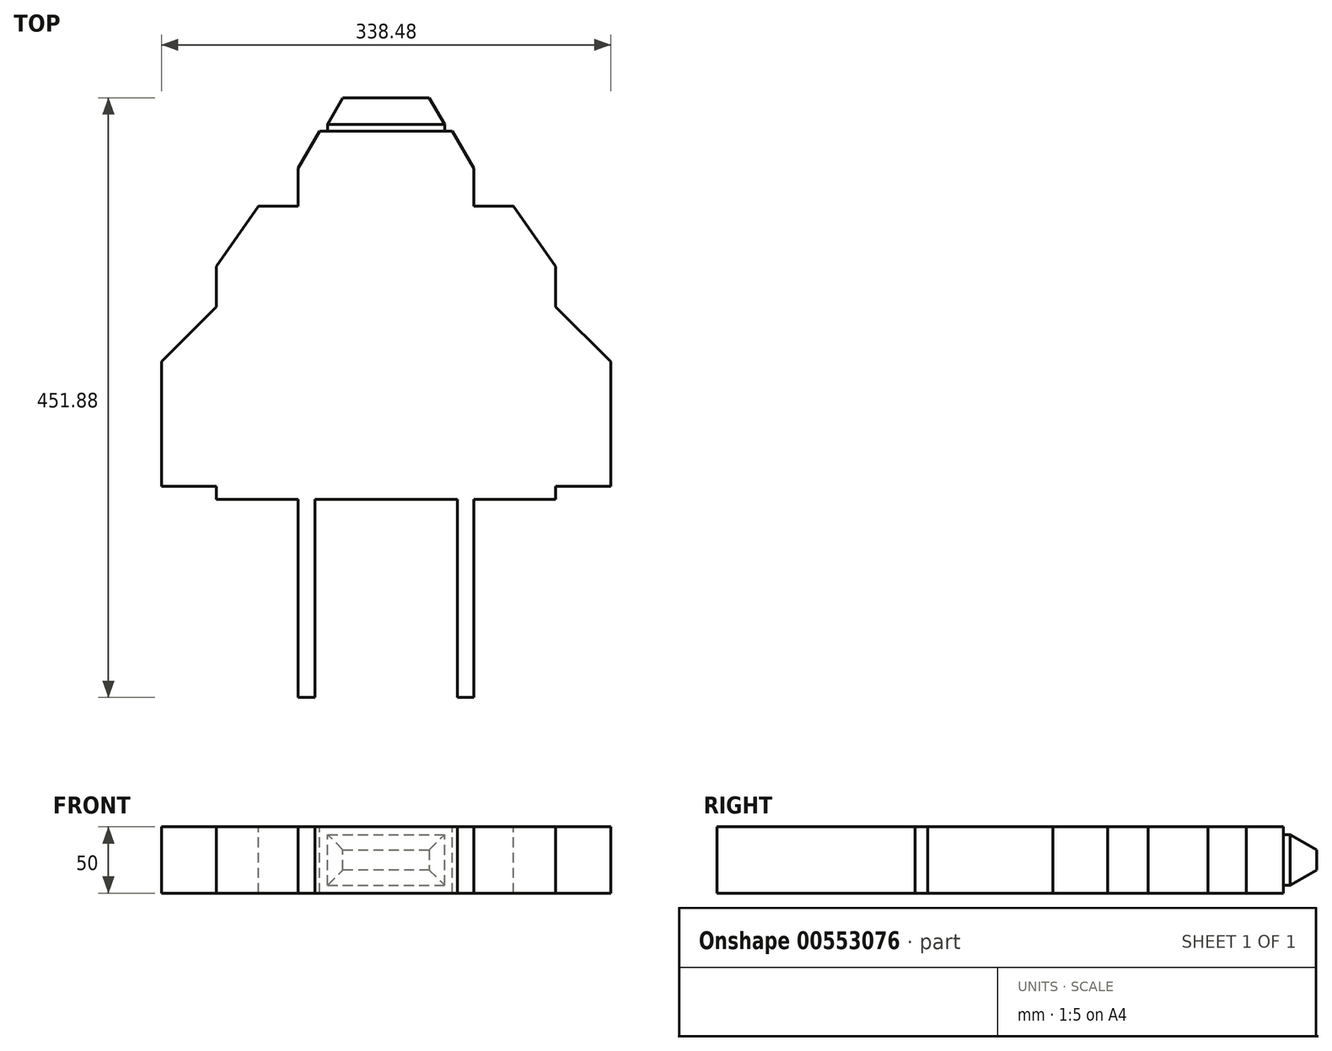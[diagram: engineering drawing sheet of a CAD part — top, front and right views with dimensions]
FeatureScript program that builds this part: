
annotation { "Feature Type Name" : "Feature", "Feature Type Description" : "" }
export const myFeature = defineFeature(function(context is Context, id is Id, definition is map)
    precondition{}
    {
        {
            var Q0;
            Q0=qCreatedBy(makeId("Top.planeOp"),FACE);
            var sketch = newSketch(context, id + "F0", { "sketchPlane" : qUnion([Q0])});
            skLineSegment(sketch, "E0", {"start": v(0, 218.46) * mm, "end": v(-50, 218.46) * mm});
            skLineSegment(sketch, "E1", {"start": v(-50, 218.46) * mm, "end": v(-66.23, 190.36) * mm});
            skLineSegment(sketch, "E2", {"start": v(-66.23, 190.36) * mm, "end": v(-66.23, 0) * mm});
            skLineSegment(sketch, "E3.MirrorCS", {"start": v(66.23, 190.36) * mm, "end": v(66.23, 0) * mm});
            skLineSegment(sketch, "E4.MirrorCS", {"start": v(0, 218.46) * mm, "end": v(50, 218.46) * mm});
            skLineSegment(sketch, "E5.MirrorCS", {"start": v(50, 218.46) * mm, "end": v(66.23, 190.36) * mm});
            skLineSegment(sketch, "E6", {"start": v(-50, 218.46) * mm, "end": v(-50, 0) * mm, "construction": true});
            skLineSegment(sketch, "E7", {"start": v(-66.23, 0) * mm, "end": v(-66.23, -208.42) * mm});
            skLineSegment(sketch, "E8", {"start": v(-66.23, -208.42) * mm, "end": v(-53.7, -208.42) * mm});
            skLineSegment(sketch, "E9", {"start": v(-53.7, -208.42) * mm, "end": v(-53.7, -59.28) * mm});
            skLineSegment(sketch, "E10", {"start": v(-53.7, -59.28) * mm, "end": v(0, -59.28) * mm});
            skLineSegment(sketch, "E11.MirrorCS", {"start": v(66.23, -208.42) * mm, "end": v(53.7, -208.42) * mm});
            skLineSegment(sketch, "E12.MirrorCS", {"start": v(66.23, 0) * mm, "end": v(66.23, -208.42) * mm});
            skLineSegment(sketch, "E13.MirrorCS", {"start": v(53.7, -59.28) * mm, "end": v(0, -59.28) * mm});
            skLineSegment(sketch, "E14.MirrorCS", {"start": v(53.7, -208.42) * mm, "end": v(53.7, -59.28) * mm});
            skLineSegment(sketch, "E15", {"start": v(-66.23, 161.65) * mm, "end": v(-96.05, 161.65) * mm});
            skLineSegment(sketch, "E16", {"start": v(-96.05, 161.65) * mm, "end": v(-127.76, 116.36) * mm});
            skLineSegment(sketch, "E17", {"start": v(-127.76, 116.36) * mm, "end": v(-127.76, -59.28) * mm});
            skLineSegment(sketch, "E18", {"start": v(-53.7, -59.28) * mm, "end": v(-66.23, -59.28) * mm, "construction": true});
            skLineSegment(sketch, "E19", {"start": v(-127.76, -59.28) * mm, "end": v(-66.23, -59.28) * mm});
            skLineSegment(sketch, "E20", {"start": v(-127.76, 86.04) * mm, "end": v(-169.24, 44.56) * mm});
            skLineSegment(sketch, "E21", {"start": v(-169.24, 44.56) * mm, "end": v(-169.24, -49.47) * mm});
            skLineSegment(sketch, "E22", {"start": v(-169.24, -49.47) * mm, "end": v(-127.76, -49.47) * mm});
            skLineSegment(sketch, "E23", {"start": v(-96.05, 161.65) * mm, "end": v(-96.05, 118.1) * mm, "construction": true});
            skLineSegment(sketch, "E24.MirrorCS", {"start": v(96.05, 161.65) * mm, "end": v(127.76, 116.36) * mm});
            skLineSegment(sketch, "E25.MirrorCS", {"start": v(127.76, 86.04) * mm, "end": v(169.24, 44.56) * mm});
            skLineSegment(sketch, "E26.MirrorCS", {"start": v(169.24, -49.47) * mm, "end": v(127.76, -49.47) * mm});
            skLineSegment(sketch, "E27.MirrorCS", {"start": v(96.05, 161.65) * mm, "end": v(96.05, 118.1) * mm, "construction": true});
            skLineSegment(sketch, "E28.MirrorCS", {"start": v(169.24, 44.56) * mm, "end": v(169.24, -49.47) * mm});
            skLineSegment(sketch, "E29.MirrorCS", {"start": v(127.76, 116.36) * mm, "end": v(127.76, -59.28) * mm});
            skLineSegment(sketch, "E30.MirrorCS", {"start": v(66.23, 161.65) * mm, "end": v(96.05, 161.65) * mm});
            skLineSegment(sketch, "E31.MirrorCS", {"start": v(127.76, -59.28) * mm, "end": v(66.23, -59.28) * mm});
            skSolve(sketch);
        }
        {
            var Q0;
            Q0=makeQuery(id+"F0.imprint","IMPRINT",FACE,{"disambiguationData":[TD([[makeQuery(id+"F0.imprint","IMPRINT",EDGE,{"derivedFrom":sQuery(id+"F0.wireOp",EDGE,"E0")}),1.0]])]});
            var Q1;
            {var subQ5=sQuery(id+"F0.wireOp",EDGE,"E15");Q1=makeQuery(id+"F0.imprint","IMPRINT",FACE,{"disambiguationData":[TD([[makeQuery(id+"F0.imprint","IMPRINT",EDGE,{"derivedFrom":subQ5}),1.0]])]});}
            var Q2;
            {var subQ0=sQuery(id+"F0.wireOp",EDGE,"E20");Q2=makeQuery(id+"F0.imprint","IMPRINT",FACE,{"disambiguationData":[TD([[makeQuery(id+"F0.imprint","IMPRINT",EDGE,{"derivedFrom":subQ0}),1.0]])]});}
            var Q3;
            {var subQ1=sQuery(id+"F0.wireOp",EDGE,"E24.MirrorCS");Q3=makeQuery(id+"F0.imprint","IMPRINT",FACE,{"disambiguationData":[TD([[makeQuery(id+"F0.imprint","IMPRINT",EDGE,{"derivedFrom":subQ1}),-1.0]])]});}
            var Q4;
            {var subQ0=sQuery(id+"F0.wireOp",EDGE,"E25.MirrorCS");Q4=makeQuery(id+"F0.imprint","IMPRINT",FACE,{"disambiguationData":[TD([[makeQuery(id+"F0.imprint","IMPRINT",EDGE,{"derivedFrom":subQ0}),-1.0]])]});}
            extrude(context, id + "F1", {"entities" : qUnion([Q0, Q1, Q2, Q3, Q4]), "oppositeDirection" : true, "depth" : 50 * mm, "offsetDistance" : 25 * mm});
        }
        {
            var Q0;
            Q0=makeQuery(id+"F1.opExtrude","SWEPT_FACE",FACE,{"disambiguationData":[OSD([sQuery(id+"F0.wireOp",EDGE,"E0"),sQuery(id+"F0.wireOp",EDGE,"E4.MirrorCS")])]});
            var sketch = newSketch(context, id + "F2", { "sketchPlane" : qUnion([Q0])});
            skLineSegment(sketch, "E32.0", {"start": v(44.1, -5.9) * mm, "end": v(-44.1, -5.9) * mm});
            skLineSegment(sketch, "E32.1", {"start": v(44.1, -44.1) * mm, "end": v(44.1, -5.9) * mm});
            skLineSegment(sketch, "E32.2", {"start": v(44.1, -44.1) * mm, "end": v(-44.1, -44.1) * mm});
            skLineSegment(sketch, "E32.3", {"start": v(-44.1, -44.1) * mm, "end": v(-44.1, -5.9) * mm});
            skLineSegment(sketch, "E33", {"start": v(0, 0) * mm, "end": v(0, -50) * mm, "construction": true});
            skLineSegment(sketch, "E34.bottom", {"start": v(-21.56, -17.06) * mm, "end": v(21.56, -17.06) * mm});
            skLineSegment(sketch, "E34.top", {"start": v(-21.56, -32.94) * mm, "end": v(21.56, -32.94) * mm});
            skLineSegment(sketch, "E34.left", {"start": v(-21.56, -17.06) * mm, "end": v(-21.56, -32.94) * mm});
            skLineSegment(sketch, "E34.right", {"start": v(21.56, -17.06) * mm, "end": v(21.56, -32.94) * mm});
            skPoint(sketch, "E34.middle", {"position": v(0, -25) * mm});
            skSolve(sketch);
        }
        {
            var Q0;
            Q0=makeQuery(id+"F2.imprint","IMPRINT",FACE,{"disambiguationData":[TD([[makeQuery(id+"F2.imprint","IMPRINT",EDGE,{"derivedFrom":sQuery(id+"F2.wireOp",EDGE,"E32.0")}),1.0]])]});
            var Q1;
            Q1=makeQuery(id+"F2.imprint","IMPRINT",FACE,{"disambiguationData":[TD([[makeQuery(id+"F2.imprint","IMPRINT",EDGE,{"derivedFrom":sQuery(id+"F2.wireOp",EDGE,"E34.bottom")}),-1.0]])]});
            extrude(context, id + "F3", {"entities" : qUnion([Q0, Q1]), "operationType" : NewBodyOperationType.ADD, "depth" : 25 * mm, "offsetDistance" : 25 * mm});
        }
        {
            var Q0;
            Q0=makeQuery(id+"F3.opExtrude","CAP_FACE",FACE,{"disambiguationData":[OSD([sQuery(id+"F2.wireOp",EDGE,"E32.0"),sQuery(id+"F2.wireOp",EDGE,"E32.1"),sQuery(id+"F2.wireOp",EDGE,"E32.2"),sQuery(id+"F2.wireOp",EDGE,"E32.3")])],"isStart":false});
            chamfer(context, id + "F4", {"entities" : qUnion([Q0]), "chamferType" : ChamferType.OFFSET_ANGLE, "width" : 20 * mm, "oppositeDirection" : true, "angle" : 30 * degree, "tangentPropagation" : true});
        }
    });
